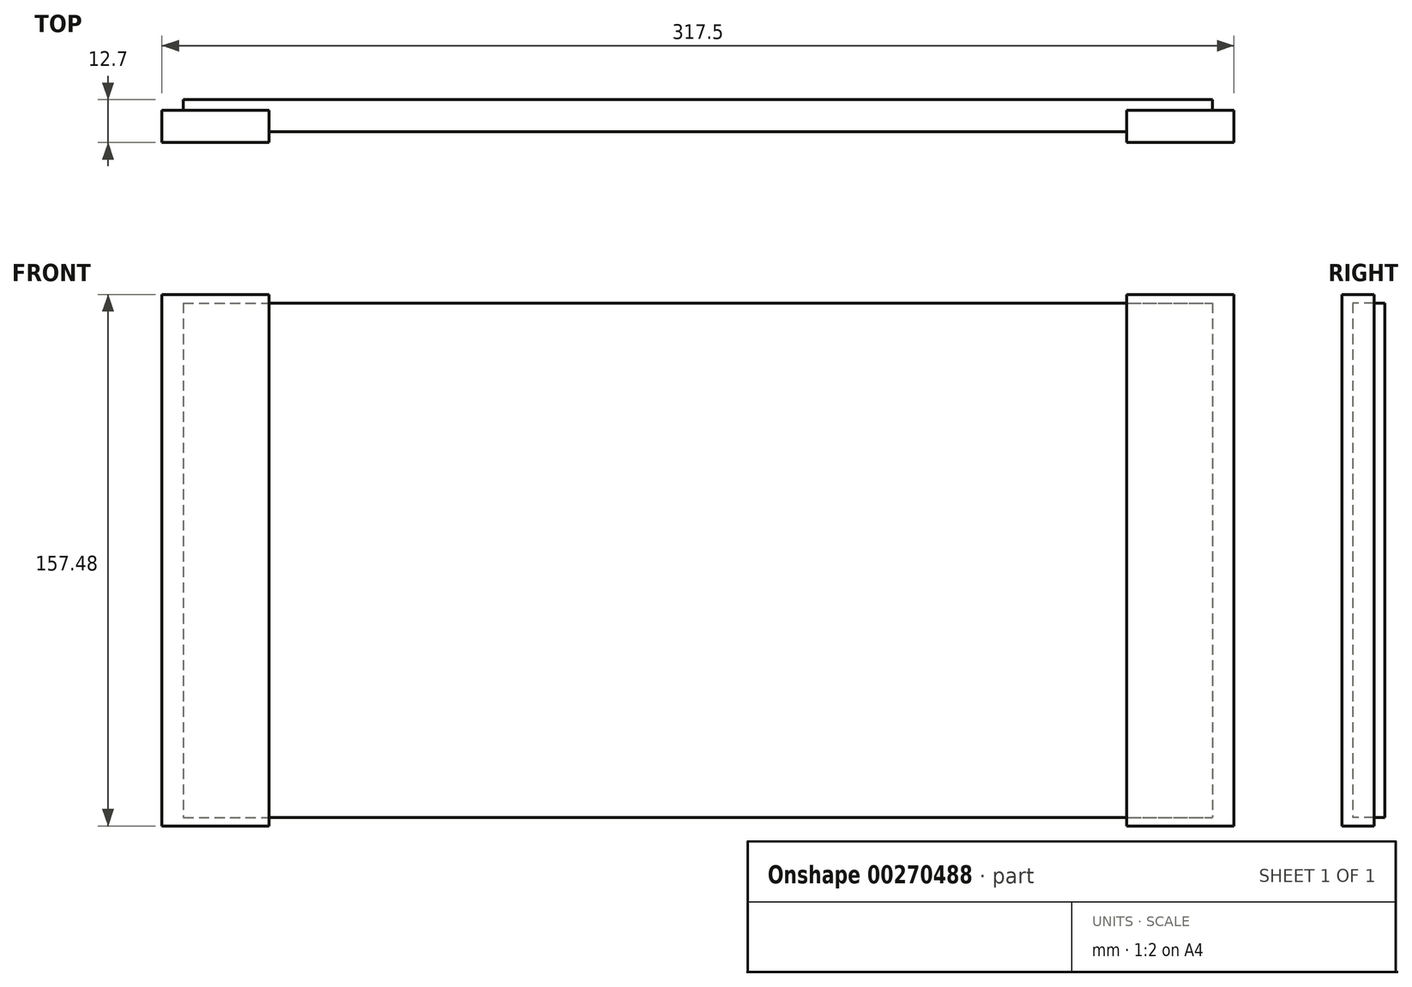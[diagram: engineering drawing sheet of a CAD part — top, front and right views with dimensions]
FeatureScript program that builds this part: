
annotation { "Feature Type Name" : "Feature", "Feature Type Description" : "" }
export const myFeature = defineFeature(function(context is Context, id is Id, definition is map)
    precondition{}
    {
        {
            var Q0;
            Q0=qCreatedBy(makeId("Front.planeOp"),FACE);
            var sketch = newSketch(context, id + "F0", { "sketchPlane" : qUnion([Q0])});
            skLineSegment(sketch, "E0.bottom", {"start": v(-152.4, 76.2) * mm, "end": v(152.4, 76.2) * mm});
            skLineSegment(sketch, "E0.top", {"start": v(-152.4, -76.2) * mm, "end": v(152.4, -76.2) * mm});
            skLineSegment(sketch, "E0.left", {"start": v(-152.4, 76.2) * mm, "end": v(-152.4, -76.2) * mm});
            skLineSegment(sketch, "E0.right", {"start": v(152.4, 76.2) * mm, "end": v(152.4, -76.2) * mm});
            skSolve(sketch);
        }
        {
            var Q0;
            Q0=makeQuery(id+"F0.imprint","IMPRINT",FACE,{"disambiguationData":[TD([[makeQuery(id+"F0.imprint","IMPRINT",EDGE,{"derivedFrom":sQuery(id+"F0.wireOp",EDGE,"E0.bottom")}),-1.0]])]});
            extrude(context, id + "F1", {"entities" : qUnion([Q0]), "depth" : 9.52 * mm});
        }
        {
            var Q0;
            Q0=makeQuery(id+"F1.opExtrude","CAP_FACE",FACE,{"disambiguationData":[OSD([sQuery(id+"F0.wireOp",EDGE,"E0.bottom"),sQuery(id+"F0.wireOp",EDGE,"E0.top"),sQuery(id+"F0.wireOp",EDGE,"E0.left"),sQuery(id+"F0.wireOp",EDGE,"E0.right")])],"isStart":false});
            var sketch = newSketch(context, id + "F2", { "sketchPlane" : qUnion([Q0])});
            skLineSegment(sketch, "E1.bottom", {"start": v(-158.75, 78.74) * mm, "end": v(-127, 78.74) * mm});
            skLineSegment(sketch, "E1.top", {"start": v(-158.75, -78.74) * mm, "end": v(-127, -78.74) * mm});
            skLineSegment(sketch, "E1.left", {"start": v(-158.75, 78.74) * mm, "end": v(-158.75, -78.74) * mm});
            skLineSegment(sketch, "E1.right", {"start": v(-127, 78.74) * mm, "end": v(-127, -78.74) * mm});
            skLineSegment(sketch, "E2", {"start": v(0, 81.98) * mm, "end": v(0, -111.21) * mm, "construction": true});
            skLineSegment(sketch, "E3.MirrorCS", {"start": v(158.75, 78.74) * mm, "end": v(127, 78.74) * mm});
            skLineSegment(sketch, "E4.MirrorCS", {"start": v(158.75, 78.74) * mm, "end": v(158.75, -78.74) * mm});
            skLineSegment(sketch, "E5.MirrorCS", {"start": v(127, 78.74) * mm, "end": v(127, -78.74) * mm});
            skLineSegment(sketch, "E6.MirrorCS", {"start": v(158.75, -78.74) * mm, "end": v(127, -78.74) * mm});
            skSolve(sketch);
        }
        {
            var Q0;
            {var subQ1=sQuery(id+"F2.wireOp",EDGE,"E1.bottom");Q0=makeQuery(id+"F2.imprint","IMPRINT",FACE,{"disambiguationData":[TD([[makeQuery(id+"F2.imprint","IMPRINT",EDGE,{"derivedFrom":subQ1}),-1.0]])]});}
            var Q1;
            {var subQ5=makeQuery(id+"F1.opExtrude","CAP_EDGE",EDGE,{"disambiguationData":[OSD([sQuery(id+"F0.wireOp",EDGE,"E0.left")])],"isStart":false});Q1=makeQuery(id+"F2.imprint","IMPRINT",FACE,{"disambiguationData":[TD([[makeQuery(id+"F2.imprint","IMPRINT",EDGE,{"derivedFrom":subQ5}),1.0]])]});}
            var Q2;
            {var subQ5=makeQuery(id+"F1.opExtrude","CAP_EDGE",EDGE,{"disambiguationData":[OSD([sQuery(id+"F0.wireOp",EDGE,"E0.right")])],"isStart":false});Q2=makeQuery(id+"F2.imprint","IMPRINT",FACE,{"disambiguationData":[TD([[makeQuery(id+"F2.imprint","IMPRINT",EDGE,{"derivedFrom":subQ5}),-1.0]])]});}
            var Q3;
            {var subQ4=sQuery(id+"F2.wireOp",EDGE,"E3.MirrorCS");Q3=makeQuery(id+"F2.imprint","IMPRINT",FACE,{"disambiguationData":[TD([[makeQuery(id+"F2.imprint","IMPRINT",EDGE,{"derivedFrom":subQ4}),1.0]])]});}
            extrude(context, id + "F3", {"entities" : qUnion([Q0, Q1, Q2, Q3]), "oppositeDirection" : true, "depth" : 6.35 * mm, "hasSecondDirection" : true, "secondDirectionOppositeDirection" : false, "secondDirectionDepth" : 3.17 * mm});
        }
        {
            var Q0;
            Q0=makeQuery(id+"F3.opExtrude","SWEPT_BODY",BODY,{"disambiguationData":[OSD([sQuery(id+"F2.wireOp",EDGE,"E1.bottom"),sQuery(id+"F2.wireOp",EDGE,"E1.top"),sQuery(id+"F2.wireOp",EDGE,"E1.left"),sQuery(id+"F2.wireOp",EDGE,"E1.right")])]});
            var Q1;
            Q1=makeQuery(id+"F3.opExtrude","SWEPT_BODY",BODY,{"disambiguationData":[OSD([sQuery(id+"F2.wireOp",EDGE,"E3.MirrorCS"),sQuery(id+"F2.wireOp",EDGE,"E4.MirrorCS"),sQuery(id+"F2.wireOp",EDGE,"E5.MirrorCS"),sQuery(id+"F2.wireOp",EDGE,"E6.MirrorCS")])]});
            var Q2;
            Q2=makeQuery(id+"F1.opExtrude","SWEPT_BODY",BODY,{"disambiguationData":[OSD([sQuery(id+"F0.wireOp",EDGE,"E0.bottom"),sQuery(id+"F0.wireOp",EDGE,"E0.top"),sQuery(id+"F0.wireOp",EDGE,"E0.left"),sQuery(id+"F0.wireOp",EDGE,"E0.right")])]});
            booleanBodies(context, id + "F4", {"operationType" : BooleanOperationType.SUBTRACTION, "tools" : qUnion([Q0, Q1]), "targets" : qUnion([Q2]), "keepTools" : true});
        }
    });
